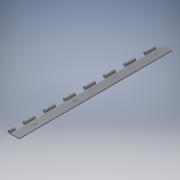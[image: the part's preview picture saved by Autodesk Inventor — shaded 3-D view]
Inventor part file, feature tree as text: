
AUTODESK INVENTOR PART (.ipt)
format: ipt  version: 2016 (Build 200138000, 138)  size: 184,832 bytes
history: native  units: mm
features: sketch x3, extrude x2, pattern_linear x1, hole x1
ambient origin geometry x8: Origin, YZ Plane, XZ Plane, XY Plane, X Axis, Y Axis, Z Axis, Center Point
bodies: Solid1 (feature_tree)
feature tree (7):
  extrude  "Extrusion1"  Depth=3.0mm
  extrude  "Extrusion2"  Depth=10.0mm
  pattern_linear  "Rectangular Pattern1"  Count1=2  [1 undecoded]
  hole  "Hole1"  [1 undecoded]
  sketch  "Sketch2"  dims[d0=1.5mm d1=1.5mm d2=20.0mm d3=3.0mm d4=4.712389mm]
  sketch  "Sketch3"  dims[d5=304.8mm d6=0.0mm d7=10.0mm d8=20.0mm]
  sketch  "Sketch4"  dims[d9=6.0mm d10=1800.0mm d11=0.0mm d12=250.0mm d14=40.0mm d15=8.0mm d16=3.0mm d17=6.0mm d18=6.0mm d19=2.0mm d20=90.0deg d21=8.0mm d22=20.594885mm]
note: 2 required parameter values undecoded (feature->parameter linkage not recoverable at this tier; creation-order binding heuristic only, values carry confidence <= 0.55)
